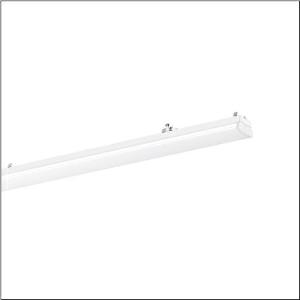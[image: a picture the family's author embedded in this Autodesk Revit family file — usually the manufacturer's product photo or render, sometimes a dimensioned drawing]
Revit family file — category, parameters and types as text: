
# Revit family: licross_r__11_recessed_opal_mo_51tl1d7n48xg_8506
name_source: partatom
category: Lighting Fixtures
units: mm (PartAtom-declared; Revit-internal decimal feet)

## family parameters
Cut with Voids When Loaded = No
Host = Face
Light Source = No
Part Type = Normal
Room Calculation Point = No
Round Connector Dimension = Use Diameter
Shared = No

## types (1)
- Licross® 11 recessed opal MO (1 x LED, 8490 lm, 48.5 W, 4000K)
    Apparent Load = 49 VA
    CIE Flux Codes = 44 73 91 87 100
    Color Rendering = 80
    Color Temperature = 4000K
    Default Elevation = 1800 mm
    Description = Licross® 11 recessed opal MO, luminaire insert, of sheet steel, coil coated, white, length: 1.500mm, width: 76mm, height: 87mm, LED rated luminous flux: 8.490lm, light colour: 840, control gear: ON/OFF, with plug, 3-pole, with phase selection, mains connection: 220..240V, AC, 50/60Hz, rated input power: 49W, halogen-free wiring, primary optical cover: cover, of PMMA, light emission: direct with ceiling illumination distribution, primary light characteristic: symmetric, protection rating (complete): IP40, insulation class (complete): insulation class I (protective earthing), certification: CE, ENEC, VDE, UKCA, protection symbol: D if used in an environment without relevant dust loads with corresponding accessories, impact resistance: IK06, permissible ambient temperature for indoor applications: -35..+35°C, corresponds to IFS (International Featured Standards) requirements for safety and quality in the food industry, reducing of maximum allowable ambient temperature of 5°C with ceiling mounting, packaging unit: 1 piece
    Height = 83 mm
    Lamp = 1 x LED
    Lamp Light Flux = 8490 lm
    Lamp Power = 48.5 W
    Lamp count = 1
    Length = 1500 mm
    Luminous efficacy = 175 lm/W
    Manufacturer = Siteco
    ModVariant = No
    Model = 51TL1D7N48XG
    Mounting Place = Ceiling
    Mounting Type = Pendant
    Number of Poles = 1
    OnlyDefault = Yes
    Power Factor = 1
    Product Name = Licross® 11 recessed opal MO
    Product group = luminaire insert
    ProductGroupID = 901
    Protection Class = Protection class I
    Protection Degree = IP 40
    RLX_Detail_Level = 1
    RLX_Emergency_Light_Flux = 0 lm
    RLX_Emergency_Type = 0
    RLX_Emergency_Type_DB = No
    RlxData = <blob elided: 14501 chars, md5=1a784b11>
    Socket = socket
    Standby Power = 0 W
    System Light Flux = 8490 lm
    System Power = 49 W
    Type Comments = Product without accessories
    Type Image = l_1313666.jpg
    URL = http://relux.com
    VarID = ---
    Voltage = 0 V
    Weight = 0.00 kg
    Width = 76 mm

## geometry (parser evidence)
native form markers: Sweep x13
no freeform markers — native parametric forms only
